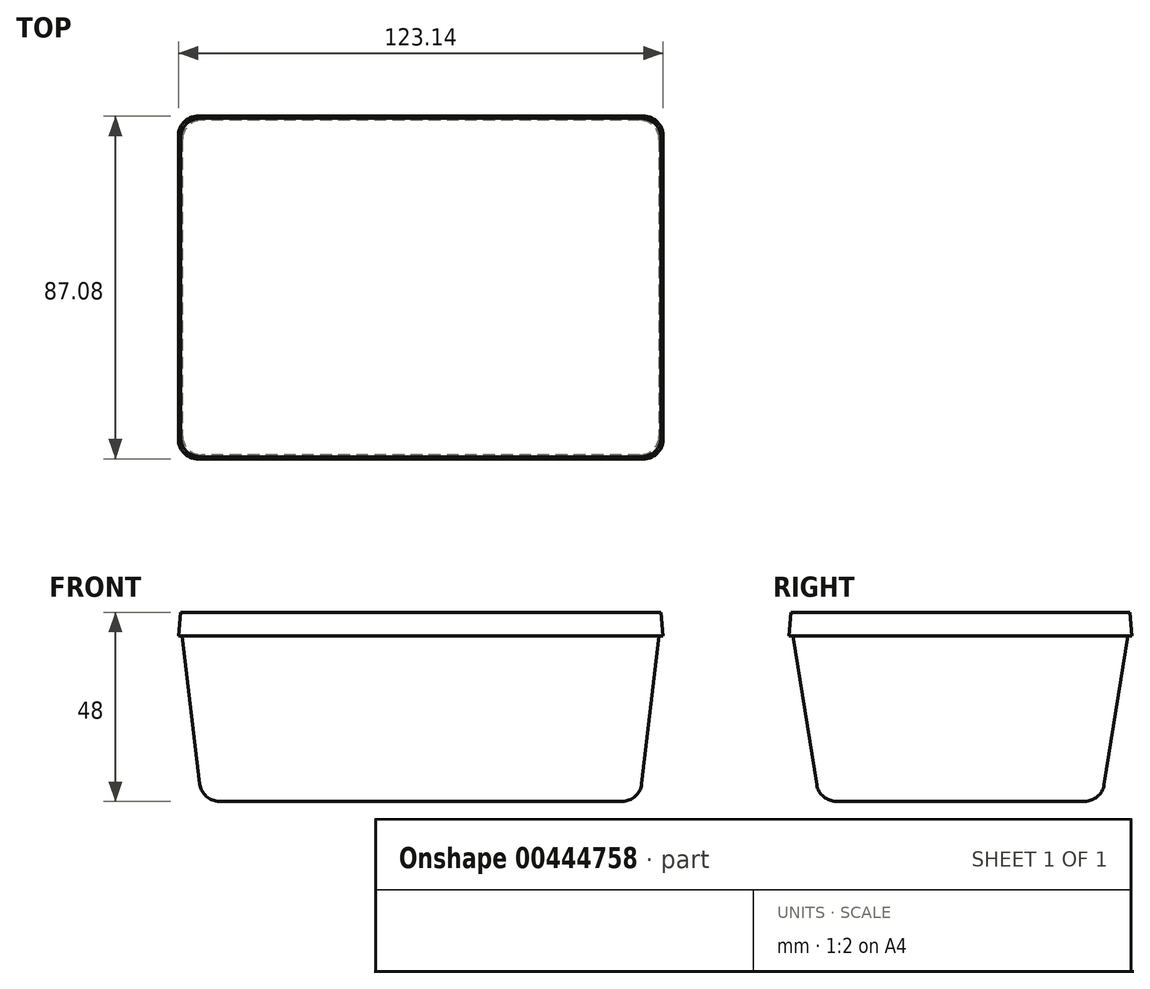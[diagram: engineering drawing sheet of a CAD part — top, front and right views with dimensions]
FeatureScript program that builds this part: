
annotation { "Feature Type Name" : "Feature", "Feature Type Description" : "" }
export const myFeature = defineFeature(function(context is Context, id is Id, definition is map)
    precondition{}
    {
        {
            var Q0;
            Q0=qCreatedBy(makeId("Top.planeOp"),FACE);
            var sketch = newSketch(context, id + "F0", { "sketchPlane" : qUnion([Q0])});
            skLineSegment(sketch, "E0.bottom", {"start": v(55.6, 35.81) * mm, "end": v(-55.6, 35.81) * mm});
            skLineSegment(sketch, "E0.top", {"start": v(55.6, -35.81) * mm, "end": v(-55.6, -35.81) * mm});
            skLineSegment(sketch, "E0.left", {"start": v(55.6, 35.81) * mm, "end": v(55.6, -35.81) * mm});
            skLineSegment(sketch, "E0.right", {"start": v(-55.6, 35.81) * mm, "end": v(-55.6, -35.81) * mm});
            skPoint(sketch, "E0.middle", {"position": v(0, 0) * mm});
            skSolve(sketch);
        }
        {
            var Q0;
            Q0=makeQuery(id+"F0.imprint","IMPRINT",FACE,{"disambiguationData":[TD([[makeQuery(id+"F0.imprint","IMPRINT",EDGE,{"derivedFrom":sQuery(id+"F0.wireOp",EDGE,"E0.bottom")}),1.0]])]});
            cPlane(context, id + "F1", {"entities" : qUnion([Q0]), "cplaneType" : CPlaneType.OFFSET, "offset" : 42 * mm, "width" : 150 * mm, "height" : 150 * mm});
        }
        {
            var Q0;
            Q0=qCreatedBy(id+"F1.planeOp",FACE);
            var sketch = newSketch(context, id + "F2", { "sketchPlane" : qUnion([Q0])});
            skLineSegment(sketch, "E1.bottom", {"start": v(60.57, 42.53) * mm, "end": v(-60.57, 42.53) * mm});
            skLineSegment(sketch, "E1.top", {"start": v(60.57, -42.53) * mm, "end": v(-60.57, -42.53) * mm});
            skLineSegment(sketch, "E1.left", {"start": v(60.57, 42.53) * mm, "end": v(60.57, -42.53) * mm});
            skLineSegment(sketch, "E1.right", {"start": v(-60.57, 42.53) * mm, "end": v(-60.57, -42.53) * mm});
            skPoint(sketch, "E1.middle", {"position": v(0, 0) * mm});
            skSolve(sketch);
        }
        {
            var Q0;
            Q0=makeQuery(id+"F0.imprint","IMPRINT",FACE,{"disambiguationData":[TD([[makeQuery(id+"F0.imprint","IMPRINT",EDGE,{"derivedFrom":sQuery(id+"F0.wireOp",EDGE,"E0.bottom")}),1.0]])]});
            var Q1;
            Q1=makeQuery(id+"F2.imprint","IMPRINT",FACE,{"disambiguationData":[TD([[makeQuery(id+"F2.imprint","IMPRINT",EDGE,{"derivedFrom":sQuery(id+"F2.wireOp",EDGE,"E1.bottom")}),1.0]])]});
            loft(context, id + "F3", {"sheetProfilesArray" : [{ "sheetProfileEntities" : qUnion([Q0]) }, { "sheetProfileEntities" : qUnion([Q1]) }]});
        }
        {
            var Q0;
            Q0=makeQuery(id+"F3.opLoft","CAP_FACE",FACE,{"disambiguationData":[OSD([makeQuery(id+"F2.imprint","IMPRINT",FACE,{"disambiguationData":[TD([[makeQuery(id+"F2.imprint","IMPRINT",EDGE,{"derivedFrom":sQuery(id+"F2.wireOp",EDGE,"E1.bottom")}),1.0]])]})])],"isStart":true});
            var sketch = newSketch(context, id + "F4", { "sketchPlane" : qUnion([Q0])});
            skLineSegment(sketch, "E2.bottom", {"start": v(-61.57, 43.54) * mm, "end": v(61.57, 43.54) * mm});
            skLineSegment(sketch, "E2.top", {"start": v(-61.57, -43.54) * mm, "end": v(61.57, -43.54) * mm});
            skLineSegment(sketch, "E2.left", {"start": v(-61.57, 43.54) * mm, "end": v(-61.57, -43.54) * mm});
            skLineSegment(sketch, "E2.right", {"start": v(61.57, 43.54) * mm, "end": v(61.57, -43.54) * mm});
            skPoint(sketch, "E2.middle", {"position": v(0, 0) * mm});
            skSolve(sketch);
        }
        {
            var Q0;
            Q0 = qSketchRegion(id + "F4", true);
            extrude(context, id + "F5", {"entities" : qUnion([Q0]), "operationType" : NewBodyOperationType.ADD, "depth" : 6 * mm});
        }
        {
            var Q0;
            Q0=makeQuery(id+"F5.opExtrude","CAP_EDGE",EDGE,{"disambiguationData":[OSD([sQuery(id+"F4.wireOp",EDGE,"E2.left")])],"isStart":false});
            var Q1;
            Q1=makeQuery(id+"F5.opExtrude","CAP_EDGE",EDGE,{"disambiguationData":[OSD([sQuery(id+"F4.wireOp",EDGE,"E2.top")])],"isStart":false});
            var Q2;
            Q2=makeQuery(id+"F5.opExtrude","CAP_EDGE",EDGE,{"disambiguationData":[OSD([sQuery(id+"F4.wireOp",EDGE,"E2.right")])],"isStart":false});
            var Q3;
            Q3=makeQuery(id+"F5.opExtrude","CAP_EDGE",EDGE,{"disambiguationData":[OSD([sQuery(id+"F4.wireOp",EDGE,"E2.bottom")])],"isStart":false});
            chamfer(context, id + "F6", {"entities" : qUnion([Q0, Q1, Q2, Q3]), "chamferType" : ChamferType.OFFSET_ANGLE, "width" : 6 * mm, "oppositeDirection" : true, "angle" : 5 * degree, "tangentPropagation" : true});
        }
        {
            var Q0;
            Q0=makeQuery(id+"F3.opLoft","SWEPT_EDGE",EDGE,{"disambiguationData":[OSD([sQuery(id+"F0.wireOp",EDGE,"E0.top"),sQuery(id+"F0.wireOp",EDGE,"E0.right"),sQuery(id+"F2.wireOp",EDGE,"E1.top"),sQuery(id+"F2.wireOp",EDGE,"E1.right")])]});
            var Q1;
            Q1=makeQuery(id+"F3.opLoft","SWEPT_EDGE",EDGE,{"disambiguationData":[OSD([sQuery(id+"F0.wireOp",EDGE,"E0.top"),sQuery(id+"F0.wireOp",EDGE,"E0.left"),sQuery(id+"F2.wireOp",EDGE,"E1.top"),sQuery(id+"F2.wireOp",EDGE,"E1.left")])]});
            var Q2;
            Q2=makeQuery(id+"F3.opLoft","SWEPT_EDGE",EDGE,{"disambiguationData":[OSD([sQuery(id+"F0.wireOp",EDGE,"E0.bottom"),sQuery(id+"F0.wireOp",EDGE,"E0.left"),sQuery(id+"F2.wireOp",EDGE,"E1.bottom"),sQuery(id+"F2.wireOp",EDGE,"E1.left")])]});
            var Q3;
            Q3=makeQuery(id+"F3.opLoft","SWEPT_EDGE",EDGE,{"disambiguationData":[OSD([sQuery(id+"F0.wireOp",EDGE,"E0.bottom"),sQuery(id+"F0.wireOp",EDGE,"E0.right"),sQuery(id+"F2.wireOp",EDGE,"E1.bottom"),sQuery(id+"F2.wireOp",EDGE,"E1.right")])]});
            fillet(context, id + "F7", {"entities" : qUnion([Q0, Q1, Q2, Q3]), "radius" : 5 * mm, "tangentPropagation" : true, "allowEdgeOverflow" : false});
        }
        {
            var Q0;
            Q0=makeQuery(id+"F3.opLoft","MID_CAP_EDGE",EDGE,{"disambiguationData":[OSD([sQuery(id+"F0.wireOp",EDGE,"E0.top"),sQuery(id+"F0.wireOp",EDGE,"E0.left"),sQuery(id+"F0.wireOp",EDGE,"E0.right")])],"capPos":0.0});
            var Q1;
            Q1=makeQuery(id+"F3.opLoft","MID_CAP_EDGE",EDGE,{"disambiguationData":[OSD([sQuery(id+"F0.wireOp",EDGE,"E0.bottom"),sQuery(id+"F0.wireOp",EDGE,"E0.top"),sQuery(id+"F0.wireOp",EDGE,"E0.left")])],"capPos":0.0});
            var Q2;
            Q2=makeQuery(id+"F3.opLoft","MID_CAP_EDGE",EDGE,{"disambiguationData":[OSD([sQuery(id+"F0.wireOp",EDGE,"E0.bottom"),sQuery(id+"F0.wireOp",EDGE,"E0.left"),sQuery(id+"F0.wireOp",EDGE,"E0.right")])],"capPos":0.0});
            var Q3;
            Q3=makeQuery(id+"F3.opLoft","MID_CAP_EDGE",EDGE,{"disambiguationData":[OSD([sQuery(id+"F0.wireOp",EDGE,"E0.bottom"),sQuery(id+"F0.wireOp",EDGE,"E0.top"),sQuery(id+"F0.wireOp",EDGE,"E0.right")])],"capPos":0.0});
            var Q4;
            {var subQ0=sQuery(id+"F0.wireOp",EDGE,"E0.top");var subQ1=sQuery(id+"F0.wireOp",EDGE,"E0.right");Q4=makeQuery(id+"F7.opFillet","BLEND_EDGE",EDGE,{"blendedFrom":[makeQuery(id+"F3.opLoft","SWEPT_EDGE",EDGE,{"disambiguationData":[OSD([subQ0,subQ1,sQuery(id+"F2.wireOp",EDGE,"E1.top"),sQuery(id+"F2.wireOp",EDGE,"E1.right")])]}),makeQuery(id+"F3.opLoft","CAP_FACE",FACE,{"disambiguationData":[OSD([makeQuery(id+"F0.imprint","IMPRINT",FACE,{"disambiguationData":[TD([[makeQuery(id+"F0.imprint","IMPRINT",EDGE,{"derivedFrom":sQuery(id+"F0.wireOp",EDGE,"E0.bottom")}),1.0]])]})])],"isStart":true})],"blendedInto":[makeQuery(id+"F3.opLoft","CAP_FACE",FACE,{"disambiguationData":[OSD([makeQuery(id+"F0.imprint","IMPRINT",FACE,{"disambiguationData":[TD([[makeQuery(id+"F0.imprint","IMPRINT",EDGE,{"derivedFrom":sQuery(id+"F0.wireOp",EDGE,"E0.bottom")}),1.0]])]})])],"isStart":true})]});}
            var Q5;
            {var subQ0=sQuery(id+"F0.wireOp",EDGE,"E0.top");var subQ1=sQuery(id+"F0.wireOp",EDGE,"E0.left");Q5=makeQuery(id+"F7.opFillet","BLEND_EDGE",EDGE,{"blendedFrom":[makeQuery(id+"F3.opLoft","SWEPT_EDGE",EDGE,{"disambiguationData":[OSD([subQ0,subQ1,sQuery(id+"F2.wireOp",EDGE,"E1.top"),sQuery(id+"F2.wireOp",EDGE,"E1.left")])]}),makeQuery(id+"F3.opLoft","CAP_FACE",FACE,{"disambiguationData":[OSD([makeQuery(id+"F0.imprint","IMPRINT",FACE,{"disambiguationData":[TD([[makeQuery(id+"F0.imprint","IMPRINT",EDGE,{"derivedFrom":sQuery(id+"F0.wireOp",EDGE,"E0.bottom")}),1.0]])]})])],"isStart":true})],"blendedInto":[makeQuery(id+"F3.opLoft","CAP_FACE",FACE,{"disambiguationData":[OSD([makeQuery(id+"F0.imprint","IMPRINT",FACE,{"disambiguationData":[TD([[makeQuery(id+"F0.imprint","IMPRINT",EDGE,{"derivedFrom":sQuery(id+"F0.wireOp",EDGE,"E0.bottom")}),1.0]])]})])],"isStart":true})]});}
            var Q6;
            {var subQ0=sQuery(id+"F0.wireOp",EDGE,"E0.bottom");var subQ1=sQuery(id+"F0.wireOp",EDGE,"E0.left");Q6=makeQuery(id+"F7.opFillet","BLEND_EDGE",EDGE,{"blendedFrom":[makeQuery(id+"F3.opLoft","SWEPT_EDGE",EDGE,{"disambiguationData":[OSD([subQ0,subQ1,sQuery(id+"F2.wireOp",EDGE,"E1.bottom"),sQuery(id+"F2.wireOp",EDGE,"E1.left")])]}),makeQuery(id+"F3.opLoft","CAP_FACE",FACE,{"disambiguationData":[OSD([makeQuery(id+"F0.imprint","IMPRINT",FACE,{"disambiguationData":[TD([[makeQuery(id+"F0.imprint","IMPRINT",EDGE,{"derivedFrom":subQ0}),1.0]])]})])],"isStart":true})],"blendedInto":[makeQuery(id+"F3.opLoft","CAP_FACE",FACE,{"disambiguationData":[OSD([makeQuery(id+"F0.imprint","IMPRINT",FACE,{"disambiguationData":[TD([[makeQuery(id+"F0.imprint","IMPRINT",EDGE,{"derivedFrom":subQ0}),1.0]])]})])],"isStart":true})]});}
            var Q7;
            {var subQ0=sQuery(id+"F0.wireOp",EDGE,"E0.bottom");var subQ1=sQuery(id+"F0.wireOp",EDGE,"E0.right");Q7=makeQuery(id+"F7.opFillet","BLEND_EDGE",EDGE,{"blendedFrom":[makeQuery(id+"F3.opLoft","SWEPT_EDGE",EDGE,{"disambiguationData":[OSD([subQ0,subQ1,sQuery(id+"F2.wireOp",EDGE,"E1.bottom"),sQuery(id+"F2.wireOp",EDGE,"E1.right")])]}),makeQuery(id+"F3.opLoft","CAP_FACE",FACE,{"disambiguationData":[OSD([makeQuery(id+"F0.imprint","IMPRINT",FACE,{"disambiguationData":[TD([[makeQuery(id+"F0.imprint","IMPRINT",EDGE,{"derivedFrom":subQ0}),1.0]])]})])],"isStart":true})],"blendedInto":[makeQuery(id+"F3.opLoft","CAP_FACE",FACE,{"disambiguationData":[OSD([makeQuery(id+"F0.imprint","IMPRINT",FACE,{"disambiguationData":[TD([[makeQuery(id+"F0.imprint","IMPRINT",EDGE,{"derivedFrom":subQ0}),1.0]])]})])],"isStart":true})]});}
            fillet(context, id + "F8", {"entities" : qUnion([Q0, Q1, Q2, Q3, Q4, Q5, Q6, Q7]), "radius" : 5 * mm, "tangentPropagation" : true, "allowEdgeOverflow" : false});
        }
        {
            var Q0;
            Q0=makeQuery(id+"F6.opChamfer","BLEND_EDGE",EDGE,{"blendedFrom":[makeQuery(id+"F5.opExtrude","CAP_EDGE",EDGE,{"disambiguationData":[OSD([sQuery(id+"F4.wireOp",EDGE,"E2.top")])],"isStart":false}),makeQuery(id+"F5.opExtrude","CAP_EDGE",EDGE,{"disambiguationData":[OSD([sQuery(id+"F4.wireOp",EDGE,"E2.left")])],"isStart":false})],"blendedInto":[]});
            var Q1;
            Q1=makeQuery(id+"F6.opChamfer","BLEND_EDGE",EDGE,{"blendedFrom":[makeQuery(id+"F5.opExtrude","CAP_EDGE",EDGE,{"disambiguationData":[OSD([sQuery(id+"F4.wireOp",EDGE,"E2.bottom")])],"isStart":false}),makeQuery(id+"F5.opExtrude","CAP_EDGE",EDGE,{"disambiguationData":[OSD([sQuery(id+"F4.wireOp",EDGE,"E2.left")])],"isStart":false})],"blendedInto":[]});
            var Q2;
            Q2=makeQuery(id+"F6.opChamfer","BLEND_EDGE",EDGE,{"blendedFrom":[makeQuery(id+"F5.opExtrude","CAP_EDGE",EDGE,{"disambiguationData":[OSD([sQuery(id+"F4.wireOp",EDGE,"E2.bottom")])],"isStart":false}),makeQuery(id+"F5.opExtrude","CAP_EDGE",EDGE,{"disambiguationData":[OSD([sQuery(id+"F4.wireOp",EDGE,"E2.right")])],"isStart":false})],"blendedInto":[]});
            var Q3;
            Q3=makeQuery(id+"F6.opChamfer","BLEND_EDGE",EDGE,{"blendedFrom":[makeQuery(id+"F5.opExtrude","CAP_EDGE",EDGE,{"disambiguationData":[OSD([sQuery(id+"F4.wireOp",EDGE,"E2.top")])],"isStart":false}),makeQuery(id+"F5.opExtrude","CAP_EDGE",EDGE,{"disambiguationData":[OSD([sQuery(id+"F4.wireOp",EDGE,"E2.right")])],"isStart":false})],"blendedInto":[]});
            fillet(context, id + "F9", {"entities" : qUnion([Q0, Q1, Q2, Q3]), "radius" : 5 * mm, "tangentPropagation" : true, "allowEdgeOverflow" : false});
        }
    });
